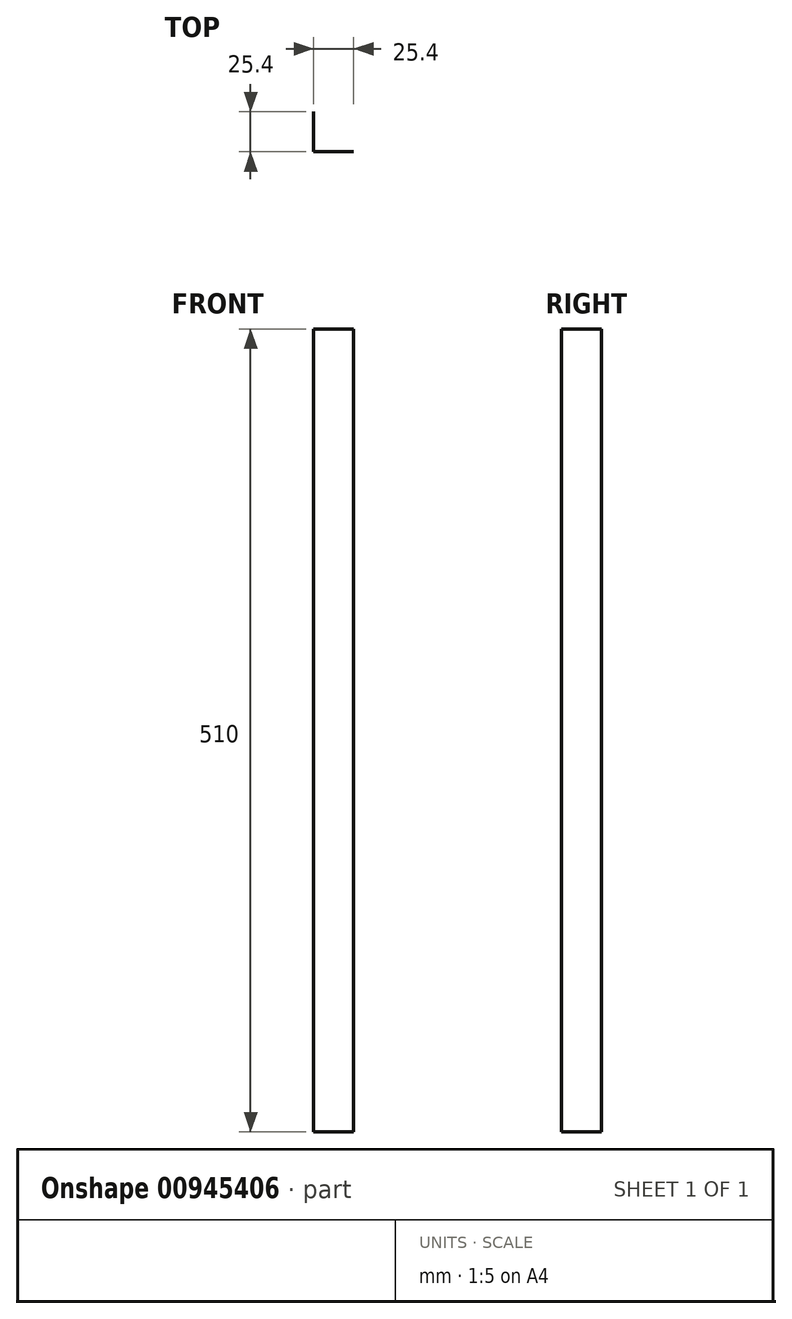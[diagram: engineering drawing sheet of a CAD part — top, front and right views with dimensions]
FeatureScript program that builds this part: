
annotation { "Feature Type Name" : "Feature", "Feature Type Description" : "" }
export const myFeature = defineFeature(function(context is Context, id is Id, definition is map)
    precondition{}
    {
        {
            var Q0;
            Q0=qCreatedBy(makeId("Top.planeOp"),FACE);
            var sketch = newSketch(context, id + "F0", { "sketchPlane" : qUnion([Q0])});
            skLineSegment(sketch, "E0.top", {"start": v(-3.35, -16.38) * mm, "end": v(22.05, -16.38) * mm});
            skLineSegment(sketch, "E0.left", {"start": v(-3.35, 9.02) * mm, "end": v(-3.35, -16.38) * mm});
            skSolve(sketch);
        }
        {
            var Q0;
            Q0=sQuery(id+"F0.wireOp",EDGE,"E0.left");
            var Q1;
            Q1=sQuery(id+"F0.wireOp",EDGE,"E0.top");
            extrude(context, id + "F1", {"bodyType" : ToolBodyType.SURFACE, "surfaceEntities" : qUnion([Q0, Q1]), "depth" : 510 * mm, "offsetDistance" : 25.4 * mm});
        }
    });
